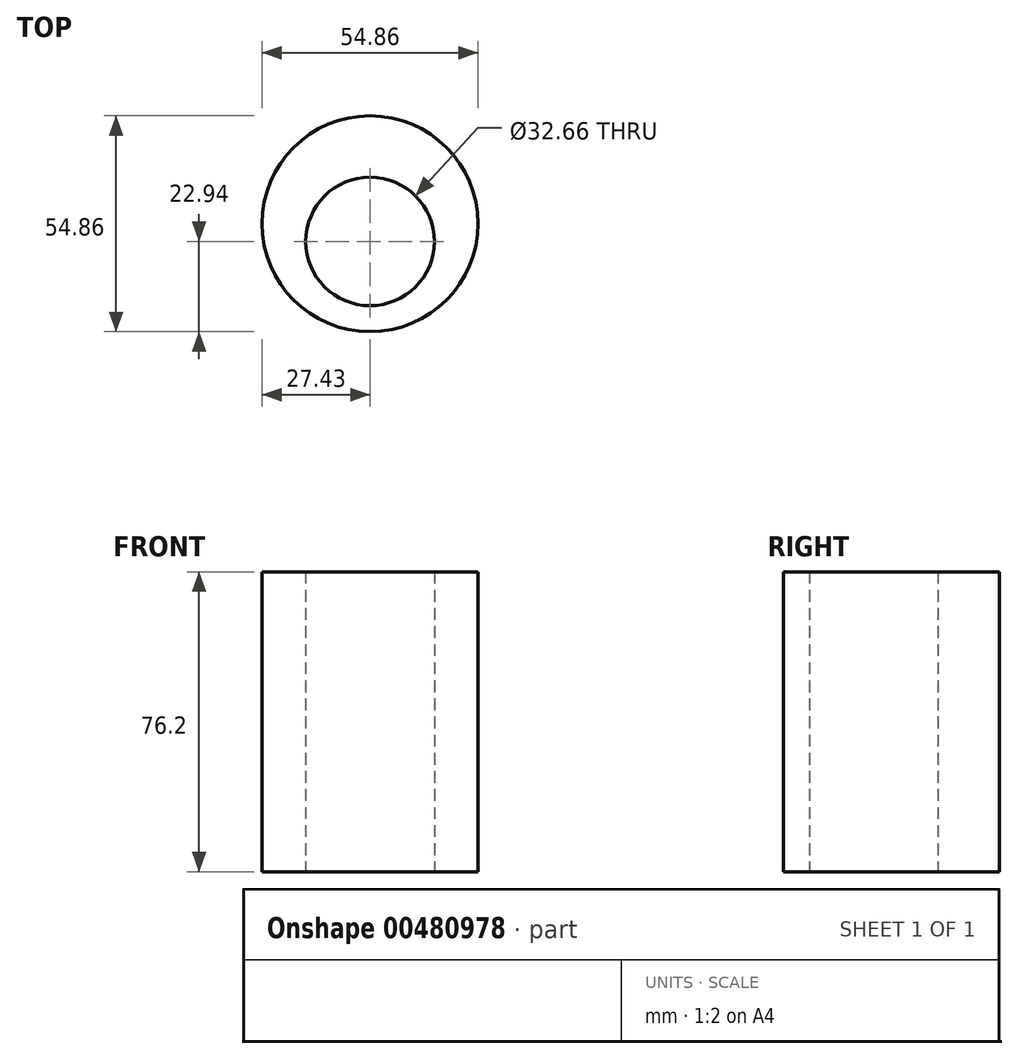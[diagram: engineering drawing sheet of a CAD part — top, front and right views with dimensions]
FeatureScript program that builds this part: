
annotation { "Feature Type Name" : "Feature", "Feature Type Description" : "" }
export const myFeature = defineFeature(function(context is Context, id is Id, definition is map)
    precondition{}
    {
        {
            var Q0;
            Q0=qCreatedBy(makeId("Top.planeOp"),FACE);
            var sketch = newSketch(context, id + "F0", { "sketchPlane" : qUnion([Q0])});
            skCircle(sketch, "E0", {"center": v(0, 4.49) * mm, "radius": 27.43 * mm});
            skCircle(sketch, "E1", {"center": v(0, 0) * mm, "radius": 16.33 * mm});
            skSolve(sketch);
        }
        {
            var Q0;
            Q0=makeQuery(id+"F0.imprint","IMPRINT",FACE,{"disambiguationData":[TD([[makeQuery(id+"F0.imprint","IMPRINT",EDGE,{"derivedFrom":sQuery(id+"F0.wireOp",EDGE,"E0")}),1.0]])]});
            extrude(context, id + "F1", {"entities" : qUnion([Q0]), "depth" : 76.2 * mm});
        }
    });
